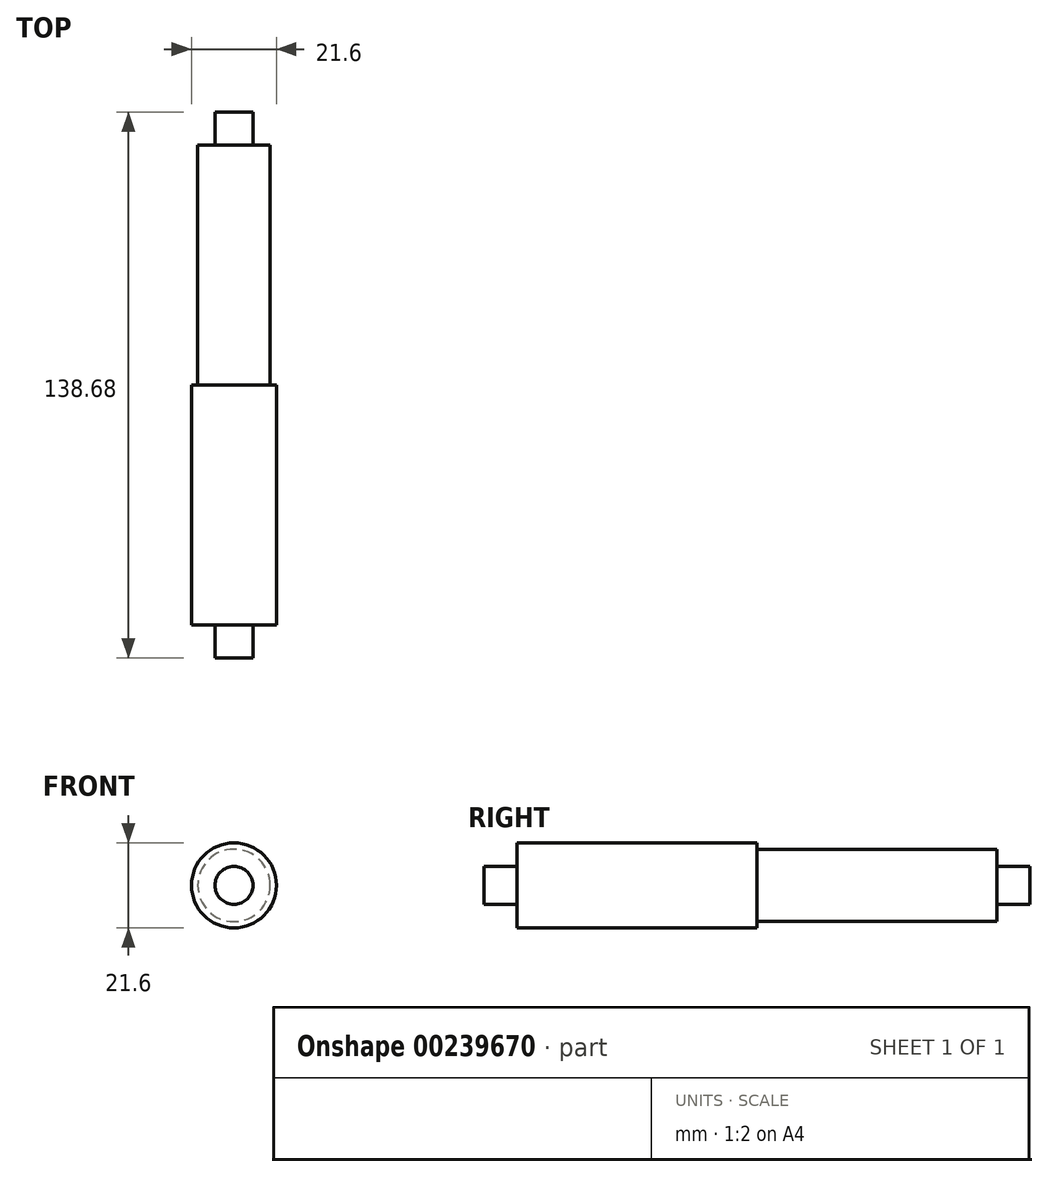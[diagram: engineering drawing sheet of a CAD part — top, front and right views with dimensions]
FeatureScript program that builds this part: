
annotation { "Feature Type Name" : "Feature", "Feature Type Description" : "" }
export const myFeature = defineFeature(function(context is Context, id is Id, definition is map)
    precondition{}
    {
        {
            var Q0;
            Q0=qCreatedBy(makeId("Front.planeOp"),FACE);
            var sketch = newSketch(context, id + "F0", { "sketchPlane" : qUnion([Q0])});
            skCircle(sketch, "E0", {"center": v(0, 0) * mm, "radius": 4.83 * mm});
            skCircle(sketch, "E1", {"center": v(0, 0) * mm, "radius": 10.8 * mm});
            skCircle(sketch, "E2", {"center": v(0, 0) * mm, "radius": 9.18 * mm});
            skSolve(sketch);
        }
        {
            var Q0;
            Q0=makeQuery(id+"F0.imprint","IMPRINT",FACE,{"disambiguationData":[TD([[makeQuery(id+"F0.imprint","IMPRINT",EDGE,{"derivedFrom":sQuery(id+"F0.wireOp",EDGE,"E1")}),1.0]])]});
            var Q1;
            Q1=makeQuery(id+"F0.imprint","IMPRINT",FACE,{"disambiguationData":[TD([[makeQuery(id+"F0.imprint","IMPRINT",EDGE,{"derivedFrom":sQuery(id+"F0.wireOp",EDGE,"E0")}),-1.0]])]});
            var Q2;
            Q2=makeQuery(id+"F0.imprint","IMPRINT",FACE,{"disambiguationData":[TD([[makeQuery(id+"F0.imprint","IMPRINT",EDGE,{"derivedFrom":sQuery(id+"F0.wireOp",EDGE,"E0")}),1.0]])]});
            extrude(context, id + "F1", {"entities" : qUnion([Q0, Q1, Q2]), "depth" : 60.96 * mm, "offsetDistance" : 25.4 * mm});
        }
        {
            var Q0;
            Q0=makeQuery(id+"F0.imprint","IMPRINT",FACE,{"disambiguationData":[TD([[makeQuery(id+"F0.imprint","IMPRINT",EDGE,{"derivedFrom":sQuery(id+"F0.wireOp",EDGE,"E0")}),1.0]])]});
            extrude(context, id + "F2", {"entities" : qUnion([Q0]), "operationType" : NewBodyOperationType.ADD, "depth" : 69.34 * mm, "offsetDistance" : 25.4 * mm});
        }
        {
            var Q0;
            Q0=makeQuery(id+"F0.imprint","IMPRINT",FACE,{"disambiguationData":[TD([[makeQuery(id+"F0.imprint","IMPRINT",EDGE,{"derivedFrom":sQuery(id+"F0.wireOp",EDGE,"E0")}),-1.0]])]});
            var Q1;
            Q1=makeQuery(id+"F0.imprint","IMPRINT",FACE,{"disambiguationData":[TD([[makeQuery(id+"F0.imprint","IMPRINT",EDGE,{"derivedFrom":sQuery(id+"F0.wireOp",EDGE,"E0")}),1.0]])]});
            extrude(context, id + "F3", {"entities" : qUnion([Q0, Q1]), "operationType" : NewBodyOperationType.ADD, "oppositeDirection" : true, "depth" : 60.96 * mm, "offsetDistance" : 25.4 * mm});
        }
        {
            var Q0;
            Q0=makeQuery(id+"F0.imprint","IMPRINT",FACE,{"disambiguationData":[TD([[makeQuery(id+"F0.imprint","IMPRINT",EDGE,{"derivedFrom":sQuery(id+"F0.wireOp",EDGE,"E0")}),1.0]])]});
            extrude(context, id + "F4", {"entities" : qUnion([Q0]), "operationType" : NewBodyOperationType.ADD, "oppositeDirection" : true, "depth" : 69.34 * mm, "offsetDistance" : 25.4 * mm});
        }
    });
